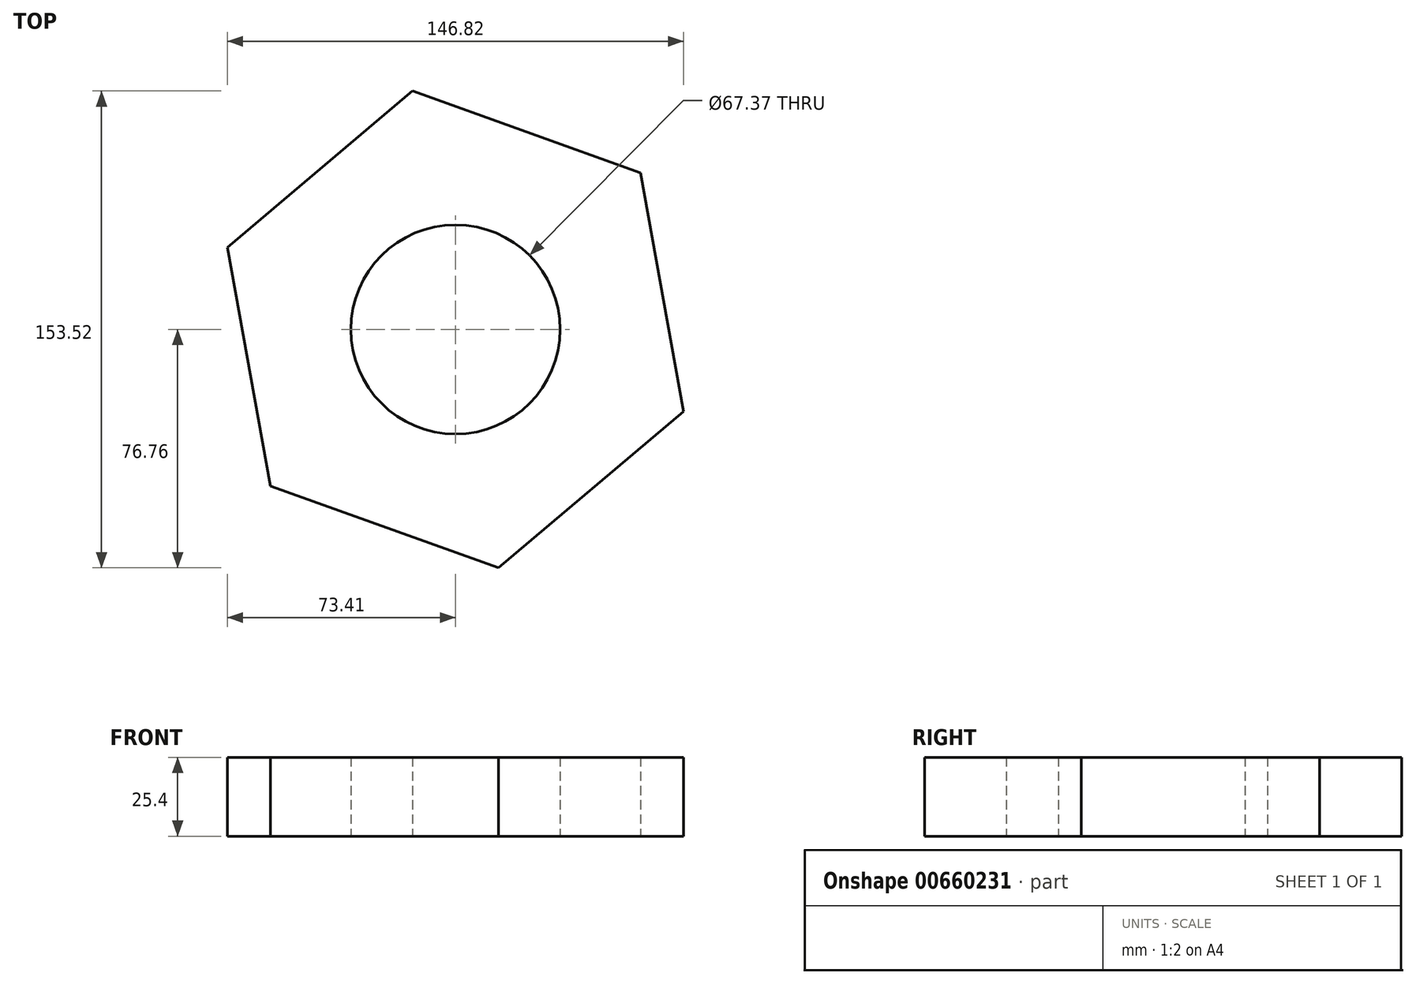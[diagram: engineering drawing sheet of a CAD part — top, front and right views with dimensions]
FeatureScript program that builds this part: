
annotation { "Feature Type Name" : "Feature", "Feature Type Description" : "" }
export const myFeature = defineFeature(function(context is Context, id is Id, definition is map)
    precondition{}
    {
        {
            var Q0;
            Q0=qCreatedBy(makeId("Top.planeOp"),FACE);
            var sketch = newSketch(context, id + "F0", { "sketchPlane" : qUnion([Q0])});
            skCircle(sketch, "E0.cCircle", {"center": v(0, 0) * mm, "radius": 67.55 * mm, "construction": true});
            skLineSegment(sketch, "E0.0", {"start": v(-13.87, 76.76) * mm, "end": v(59.54, 50.4) * mm});
            skLineSegment(sketch, "E0.1", {"start": v(59.54, 50.4) * mm, "end": v(73.41, -26.37) * mm});
            skLineSegment(sketch, "E0.2", {"start": v(73.41, -26.37) * mm, "end": v(13.87, -76.76) * mm});
            skLineSegment(sketch, "E0.3", {"start": v(13.87, -76.76) * mm, "end": v(-59.54, -50.4) * mm});
            skLineSegment(sketch, "E0.4", {"start": v(-59.54, -50.4) * mm, "end": v(-73.41, 26.37) * mm});
            skLineSegment(sketch, "E0.5", {"start": v(-73.41, 26.37) * mm, "end": v(-13.87, 76.76) * mm});
            skPoint(sketch, "E0.0.midPoint", {"position": v(22.84, 63.58) * mm});
            skCircle(sketch, "E1", {"center": v(0, 0) * mm, "radius": 33.69 * mm});
            skSolve(sketch);
        }
        {
            var Q0;
            Q0 = qSketchRegion(id + "F0", true);
            extrude(context, id + "F1", {"entities" : qUnion([Q0]), "depth" : 25.4 * mm, "offsetDistance" : 25.4 * mm});
        }
    });
